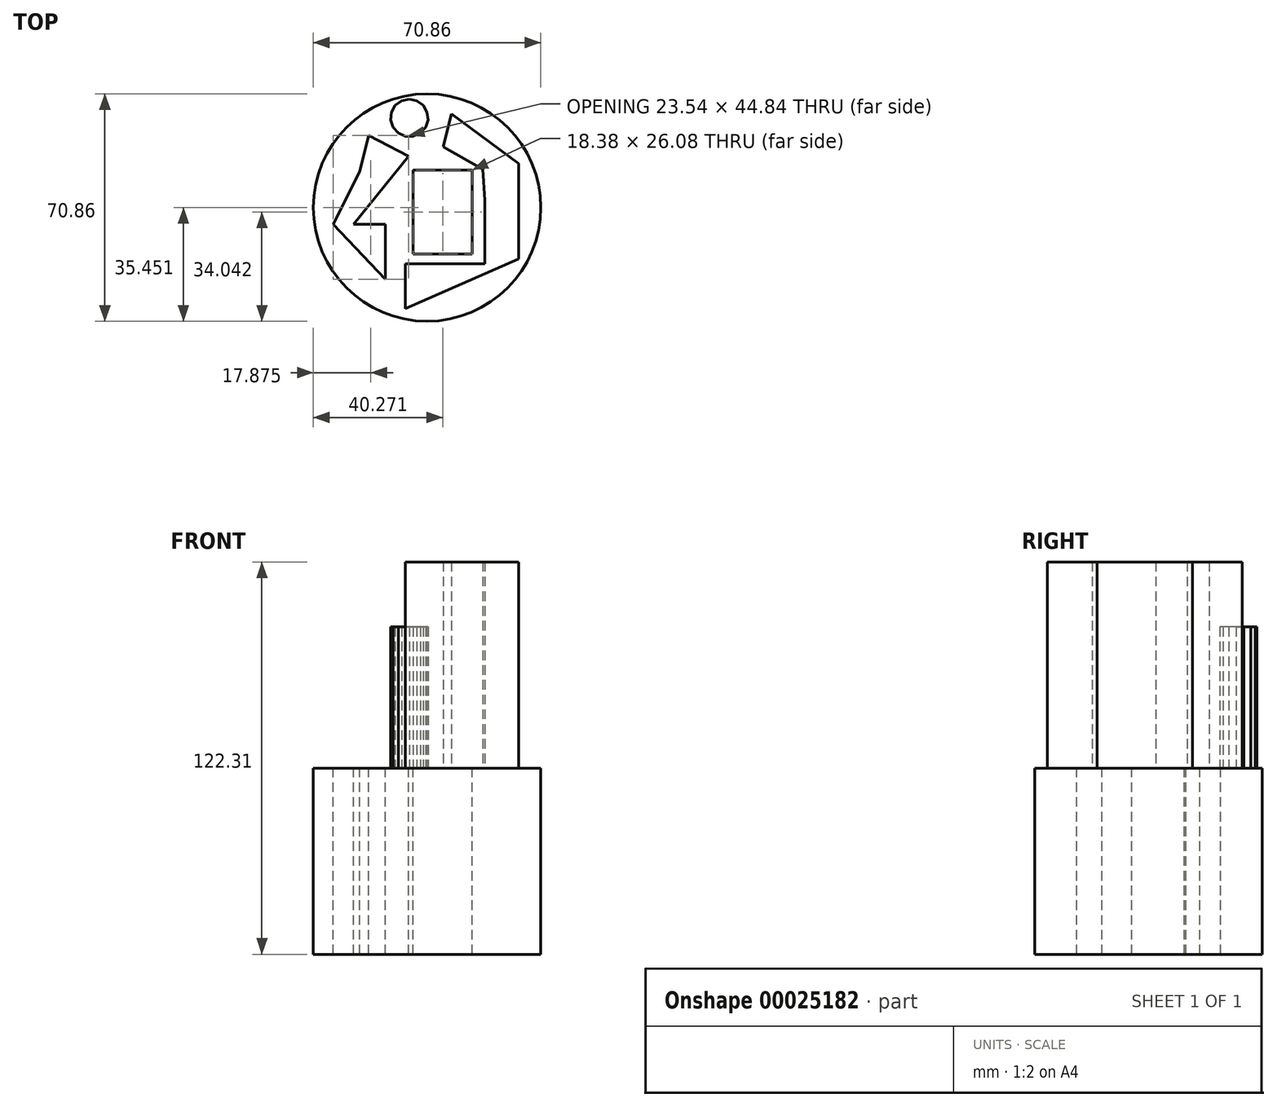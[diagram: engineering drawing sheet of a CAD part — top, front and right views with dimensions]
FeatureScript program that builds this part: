
annotation { "Feature Type Name" : "Feature", "Feature Type Description" : "" }
export const myFeature = defineFeature(function(context is Context, id is Id, definition is map)
    precondition{}
    {
        {
            var Q0;
            Q0=qCreatedBy(makeId("Top.planeOp"),FACE);
            var sketch = newSketch(context, id + "F0", { "sketchPlane" : qUnion([Q0])});
            skCircle(sketch, "E0", {"center": v(-23.47, 22.4) * mm, "radius": 35.43 * mm});
            skSolve(sketch);
        }
        {
            var Q0;
            Q0=makeQuery(id+"F0.imprint","IMPRINT",FACE,{"disambiguationData":[TD([[makeQuery(id+"F0.imprint","IMPRINT",EDGE,{"derivedFrom":sQuery(id+"F0.wireOp",EDGE,"E0")}),1.0]])]});
            extrude(context, id + "F1", {"entities" : qUnion([Q0]), "depth" : 57.97 * mm});
        }
        {
            var Q0;
            Q0=makeQuery(id+"F1.opExtrude","CAP_FACE",FACE,{"disambiguationData":[OSD([sQuery(id+"F0.wireOp",EDGE,"E0")])],"isStart":false});
            var sketch = newSketch(context, id + "F2", { "sketchPlane" : qUnion([Q0])});
            skSolve(sketch);
        }
        {
            var Q0;
            Q0=makeQuery(id+"F2.imprint","IMPRINT",FACE,{"disambiguationData":[TD([[makeQuery(id+"F2.imprint","IMPRINT",EDGE,{"derivedFrom":makeQuery(id+"F1.opExtrude","CAP_EDGE",EDGE,{"disambiguationData":[OSD([sQuery(id+"F0.wireOp",EDGE,"E0")])],"isStart":false})}),1.0]])]});
            var sketch = newSketch(context, id + "F3", { "sketchPlane" : qUnion([Q0])});
            skLineSegment(sketch, "E1.bottom", {"start": v(-27.82, 34.05) * mm, "end": v(-9.44, 34.05) * mm});
            skLineSegment(sketch, "E1.top", {"start": v(-27.82, 7.97) * mm, "end": v(-9.44, 7.97) * mm});
            skLineSegment(sketch, "E1.left", {"start": v(-27.82, 34.05) * mm, "end": v(-27.82, 7.97) * mm});
            skLineSegment(sketch, "E1.right", {"start": v(-9.44, 34.05) * mm, "end": v(-9.44, 7.97) * mm});
            skSolve(sketch);
        }
        {
            var Q0;
            Q0=makeQuery(id+"F3.imprint","IMPRINT",FACE,{"disambiguationData":[TD([[makeQuery(id+"F3.imprint","IMPRINT",EDGE,{"derivedFrom":sQuery(id+"F3.wireOp",EDGE,"E1.bottom")}),-1.0]])]});
            extrude(context, id + "F4", {"entities" : qUnion([Q0]), "operationType" : NewBodyOperationType.REMOVE, "oppositeDirection" : true, "depth" : 62.84 * mm});
        }
        {
            var Q0;
            Q0=makeQuery(id+"F2.imprint","IMPRINT",FACE,{"disambiguationData":[TD([[makeQuery(id+"F2.imprint","IMPRINT",EDGE,{"derivedFrom":makeQuery(id+"F1.opExtrude","CAP_EDGE",EDGE,{"disambiguationData":[OSD([sQuery(id+"F0.wireOp",EDGE,"E0")])],"isStart":false})}),1.0]])]});
            var sketch = newSketch(context, id + "F5", { "sketchPlane" : qUnion([Q0])});
            skCircle(sketch, "E2.cCircle", {"center": v(-43.7, 21.17) * mm, "radius": 11.06 * mm, "construction": true});
            skLineSegment(sketch, "E2.0", {"start": v(-37.55, 32.35) * mm, "end": v(-30.94, 21.43) * mm});
            skLineSegment(sketch, "E2.1", {"start": v(-30.94, 21.43) * mm, "end": v(-37.09, 10.25) * mm});
            skLineSegment(sketch, "E2.2", {"start": v(-37.09, 10.25) * mm, "end": v(-49.85, 9.98) * mm});
            skLineSegment(sketch, "E2.3", {"start": v(-49.85, 9.98) * mm, "end": v(-56.46, 20.9) * mm});
            skLineSegment(sketch, "E2.4", {"start": v(-56.46, 20.9) * mm, "end": v(-50.31, 32.09) * mm});
            skLineSegment(sketch, "E2.5", {"start": v(-50.31, 32.09) * mm, "end": v(-37.55, 32.35) * mm});
            skPoint(sketch, "E2.0.midPoint", {"position": v(-34.24, 26.9) * mm});
            skCircle(sketch, "E3.cCircle", {"center": v(-34.24, 26.9) * mm, "radius": 3.35 * mm, "construction": true});
            skLineSegment(sketch, "E3.0", {"start": v(-36.66, 29.24) * mm, "end": v(-36.12, 29.69) * mm});
            skLineSegment(sketch, "E3.1", {"start": v(-36.12, 29.69) * mm, "end": v(-35.5, 30.02) * mm});
            skLineSegment(sketch, "E3.2", {"start": v(-35.5, 30.02) * mm, "end": v(-34.82, 30.21) * mm});
            skLineSegment(sketch, "E3.3", {"start": v(-34.82, 30.21) * mm, "end": v(-34.12, 30.26) * mm});
            skLineSegment(sketch, "E3.4", {"start": v(-34.12, 30.26) * mm, "end": v(-33.42, 30.16) * mm});
            skLineSegment(sketch, "E3.5", {"start": v(-33.42, 30.16) * mm, "end": v(-32.76, 29.92) * mm});
            skLineSegment(sketch, "E3.6", {"start": v(-32.76, 29.92) * mm, "end": v(-32.16, 29.54) * mm});
            skLineSegment(sketch, "E3.7", {"start": v(-32.16, 29.54) * mm, "end": v(-31.66, 29.05) * mm});
            skLineSegment(sketch, "E3.8", {"start": v(-31.66, 29.05) * mm, "end": v(-31.27, 28.47) * mm});
            skLineSegment(sketch, "E3.9", {"start": v(-31.27, 28.47) * mm, "end": v(-31, 27.82) * mm});
            skLineSegment(sketch, "E3.10", {"start": v(-31, 27.82) * mm, "end": v(-30.88, 27.12) * mm});
            skLineSegment(sketch, "E3.11", {"start": v(-30.88, 27.12) * mm, "end": v(-30.9, 26.42) * mm});
            skLineSegment(sketch, "E3.12", {"start": v(-30.9, 26.42) * mm, "end": v(-31.08, 25.74) * mm});
            skLineSegment(sketch, "E3.13", {"start": v(-31.08, 25.74) * mm, "end": v(-31.4, 25.1) * mm});
            skLineSegment(sketch, "E3.14", {"start": v(-31.4, 25.1) * mm, "end": v(-31.82, 24.55) * mm});
            skLineSegment(sketch, "E3.15", {"start": v(-31.82, 24.55) * mm, "end": v(-32.36, 24.1) * mm});
            skLineSegment(sketch, "E3.16", {"start": v(-32.36, 24.1) * mm, "end": v(-32.99, 23.77) * mm});
            skLineSegment(sketch, "E3.17", {"start": v(-32.99, 23.77) * mm, "end": v(-33.66, 23.58) * mm});
            skLineSegment(sketch, "E3.18", {"start": v(-33.66, 23.58) * mm, "end": v(-34.37, 23.53) * mm});
            skLineSegment(sketch, "E3.19", {"start": v(-34.37, 23.53) * mm, "end": v(-35.06, 23.63) * mm});
            skLineSegment(sketch, "E3.20", {"start": v(-35.06, 23.63) * mm, "end": v(-35.72, 23.87) * mm});
            skLineSegment(sketch, "E3.21", {"start": v(-35.72, 23.87) * mm, "end": v(-36.32, 24.25) * mm});
            skLineSegment(sketch, "E3.22", {"start": v(-36.32, 24.25) * mm, "end": v(-36.82, 24.73) * mm});
            skLineSegment(sketch, "E3.23", {"start": v(-36.82, 24.73) * mm, "end": v(-37.22, 25.32) * mm});
            skLineSegment(sketch, "E3.24", {"start": v(-37.22, 25.32) * mm, "end": v(-37.48, 25.97) * mm});
            skLineSegment(sketch, "E3.25", {"start": v(-37.48, 25.97) * mm, "end": v(-37.6, 26.67) * mm});
            skLineSegment(sketch, "E3.26", {"start": v(-37.6, 26.67) * mm, "end": v(-37.57, 27.37) * mm});
            skLineSegment(sketch, "E3.27", {"start": v(-37.57, 27.37) * mm, "end": v(-37.4, 28.05) * mm});
            skLineSegment(sketch, "E3.28", {"start": v(-37.4, 28.05) * mm, "end": v(-37.1, 28.68) * mm});
            skLineSegment(sketch, "E3.29", {"start": v(-37.1, 28.68) * mm, "end": v(-36.66, 29.24) * mm});
            skPoint(sketch, "E3.0.midPoint", {"position": v(-36.39, 29.46) * mm});
            skCircle(sketch, "E4.cCircle", {"center": v(-29.02, 50.33) * mm, "radius": 5.72 * mm, "construction": true});
            skLineSegment(sketch, "E4.0", {"start": v(-27.8, 44.6) * mm, "end": v(-30.24, 44.6) * mm});
            skLineSegment(sketch, "E4.1", {"start": v(-30.24, 44.6) * mm, "end": v(-32.46, 45.6) * mm});
            skLineSegment(sketch, "E4.2", {"start": v(-32.46, 45.6) * mm, "end": v(-34.1, 47.4) * mm});
            skLineSegment(sketch, "E4.3", {"start": v(-34.1, 47.4) * mm, "end": v(-34.84, 49.71) * mm});
            skLineSegment(sketch, "E4.4", {"start": v(-34.84, 49.71) * mm, "end": v(-34.59, 52.13) * mm});
            skLineSegment(sketch, "E4.5", {"start": v(-34.59, 52.13) * mm, "end": v(-33.37, 54.24) * mm});
            skLineSegment(sketch, "E4.6", {"start": v(-33.37, 54.24) * mm, "end": v(-31.4, 55.67) * mm});
            skLineSegment(sketch, "E4.7", {"start": v(-31.4, 55.67) * mm, "end": v(-29.02, 56.18) * mm});
            skLineSegment(sketch, "E4.8", {"start": v(-29.02, 56.18) * mm, "end": v(-26.65, 55.67) * mm});
            skLineSegment(sketch, "E4.9", {"start": v(-26.65, 55.67) * mm, "end": v(-24.68, 54.24) * mm});
            skLineSegment(sketch, "E4.10", {"start": v(-24.68, 54.24) * mm, "end": v(-23.46, 52.13) * mm});
            skLineSegment(sketch, "E4.11", {"start": v(-23.46, 52.13) * mm, "end": v(-23.2, 49.71) * mm});
            skLineSegment(sketch, "E4.12", {"start": v(-23.2, 49.71) * mm, "end": v(-23.96, 47.4) * mm});
            skLineSegment(sketch, "E4.13", {"start": v(-23.96, 47.4) * mm, "end": v(-25.59, 45.6) * mm});
            skLineSegment(sketch, "E4.14", {"start": v(-25.59, 45.6) * mm, "end": v(-27.8, 44.6) * mm});
            skPoint(sketch, "E4.0.midPoint", {"position": v(-29.02, 44.6) * mm});
            skSolve(sketch);
        }
        {
            var Q0;
            Q0=makeQuery(id+"F5.imprint","IMPRINT",FACE,{"disambiguationData":[TD([[makeQuery(id+"F5.imprint","IMPRINT",EDGE,{"derivedFrom":sQuery(id+"F5.wireOp",EDGE,"E4.0")}),-1.0]])]});
            extrude(context, id + "F6", {"entities" : qUnion([Q0]), "operationType" : NewBodyOperationType.ADD, "depth" : 44.05 * mm});
        }
        {
            var Q0;
            Q0=makeQuery(id+"F2.imprint","IMPRINT",FACE,{"disambiguationData":[TD([[makeQuery(id+"F2.imprint","IMPRINT",EDGE,{"derivedFrom":makeQuery(id+"F1.opExtrude","CAP_EDGE",EDGE,{"disambiguationData":[OSD([sQuery(id+"F0.wireOp",EDGE,"E0")])],"isStart":false})}),1.0]])]});
            var sketch = newSketch(context, id + "F7", { "sketchPlane" : qUnion([Q0])});
            skLineSegment(sketch, "E5", {"start": v(-44.43, 33.56) * mm, "end": v(-52.8, 17.25) * mm});
            skLineSegment(sketch, "E6", {"start": v(-52.8, 17.25) * mm, "end": v(-36.52, 0) * mm});
            skLineSegment(sketch, "E7", {"start": v(-36.52, 0) * mm, "end": v(-36.52, 17.24) * mm});
            skLineSegment(sketch, "E8", {"start": v(-36.52, 17.24) * mm, "end": v(-46.34, 17.24) * mm});
            skLineSegment(sketch, "E9", {"start": v(-46.34, 17.24) * mm, "end": v(-29.25, 38.46) * mm});
            skLineSegment(sketch, "E10", {"start": v(-29.25, 38.46) * mm, "end": v(-41.66, 44.84) * mm});
            skLineSegment(sketch, "E11", {"start": v(-41.66, 44.84) * mm, "end": v(-44.43, 33.56) * mm});
            skSolve(sketch);
        }
        {
            var Q0;
            Q0=makeQuery(id+"F7.imprint","IMPRINT",FACE,{"disambiguationData":[TD([[makeQuery(id+"F7.imprint","IMPRINT",EDGE,{"derivedFrom":sQuery(id+"F7.wireOp",EDGE,"E5")}),1.0]])]});
            extrude(context, id + "F8", {"entities" : qUnion([Q0]), "operationType" : NewBodyOperationType.REMOVE, "oppositeDirection" : true, "depth" : 102.88 * mm});
        }
        {
            var Q0;
            Q0=makeQuery(id+"F2.imprint","IMPRINT",FACE,{"disambiguationData":[TD([[makeQuery(id+"F2.imprint","IMPRINT",EDGE,{"derivedFrom":makeQuery(id+"F1.opExtrude","CAP_EDGE",EDGE,{"disambiguationData":[OSD([sQuery(id+"F0.wireOp",EDGE,"E0")])],"isStart":false})}),1.0]])]});
            var sketch = newSketch(context, id + "F9", { "sketchPlane" : qUnion([Q0])});
            skLineSegment(sketch, "E12", {"start": v(-5.52, 24.72) * mm, "end": v(-5.52, 4.86) * mm});
            skLineSegment(sketch, "E13", {"start": v(-5.52, 4.86) * mm, "end": v(-30.28, 4.86) * mm});
            skLineSegment(sketch, "E14", {"start": v(-30.28, 4.86) * mm, "end": v(-30.28, -9.12) * mm});
            skLineSegment(sketch, "E15", {"start": v(-30.28, -9.12) * mm, "end": v(5.12, 6.37) * mm});
            skLineSegment(sketch, "E16", {"start": v(5.12, 6.37) * mm, "end": v(5.12, 36.08) * mm});
            skLineSegment(sketch, "E17", {"start": v(5.12, 36.08) * mm, "end": v(-15.92, 51.6) * mm});
            skLineSegment(sketch, "E18", {"start": v(-15.92, 51.6) * mm, "end": v(-18.46, 41.35) * mm});
            skLineSegment(sketch, "E19", {"start": v(-18.46, 41.35) * mm, "end": v(-6.14, 34.4) * mm});
            skLineSegment(sketch, "E20", {"start": v(-6.14, 34.4) * mm, "end": v(-5.52, 24.72) * mm});
            skSolve(sketch);
        }
        {
            var Q0;
            Q0=makeQuery(id+"F9.imprint","IMPRINT",FACE,{"disambiguationData":[TD([[makeQuery(id+"F9.imprint","IMPRINT",EDGE,{"derivedFrom":sQuery(id+"F9.wireOp",EDGE,"E12")}),1.0]])]});
            extrude(context, id + "F10", {"entities" : qUnion([Q0]), "operationType" : NewBodyOperationType.ADD, "depth" : 64.33 * mm});
        }
    });
